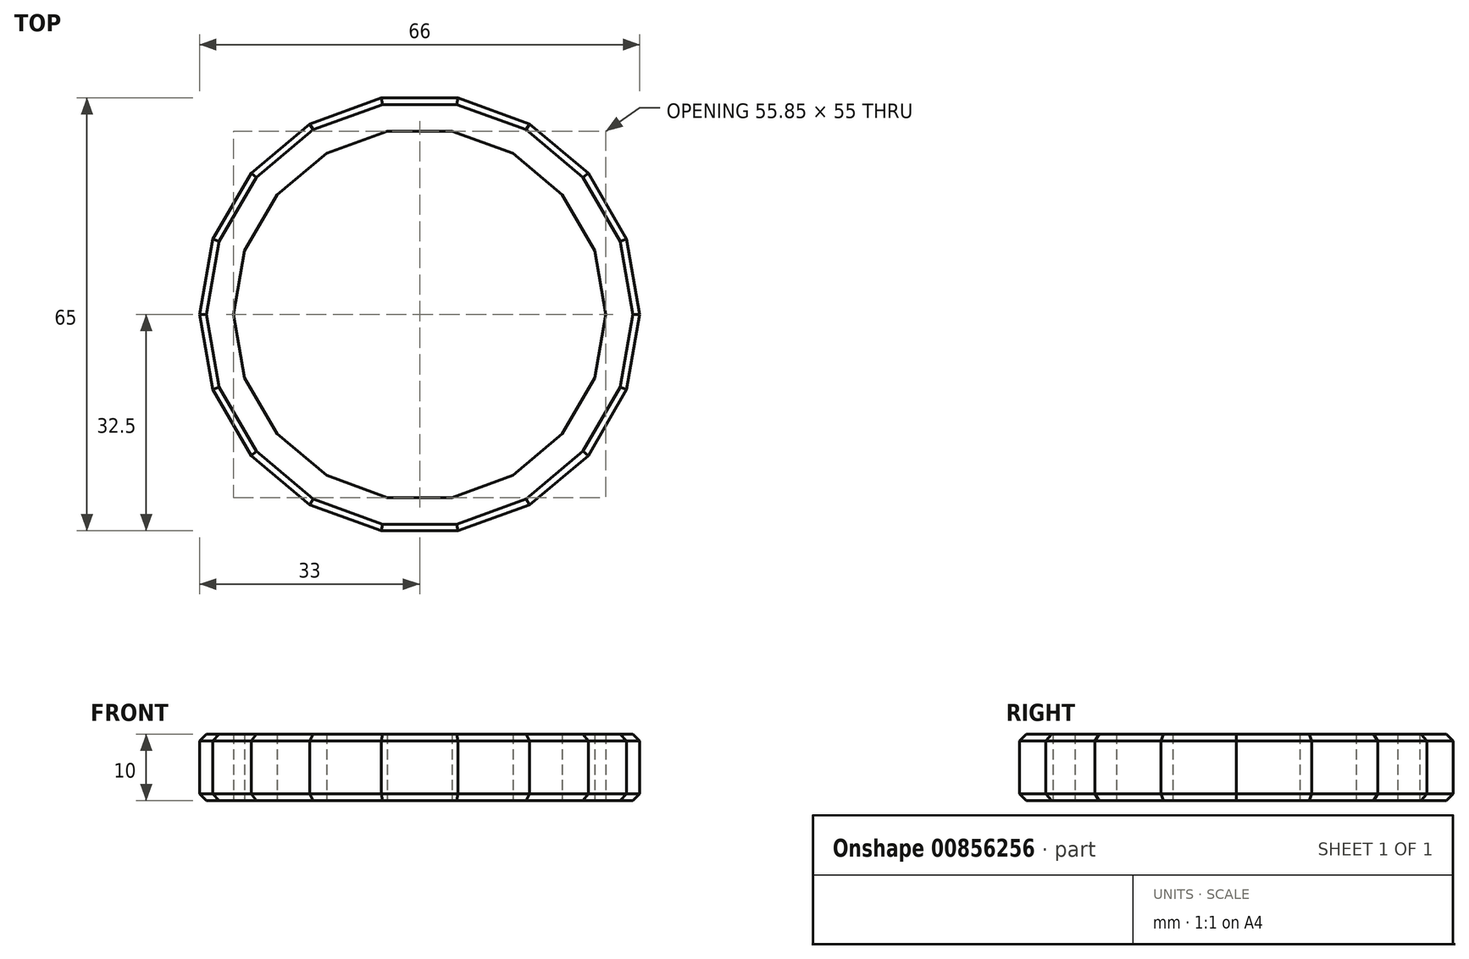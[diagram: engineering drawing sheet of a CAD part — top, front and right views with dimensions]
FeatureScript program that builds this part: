
annotation { "Feature Type Name" : "Feature", "Feature Type Description" : "" }
export const myFeature = defineFeature(function(context is Context, id is Id, definition is map)
    precondition{}
    {
        {
            var Q0;
            Q0=qCreatedBy(makeId("Top.planeOp"),FACE);
            var sketch = newSketch(context, id + "F0", { "sketchPlane" : qUnion([Q0])});
            skCircle(sketch, "E0.cCircle", {"center": v(0, 0) * mm, "radius": 27.5 * mm, "construction": true});
            skLineSegment(sketch, "E0.0", {"start": v(-4.85, 27.5) * mm, "end": v(4.85, 27.5) * mm});
            skLineSegment(sketch, "E0.1", {"start": v(4.85, 27.5) * mm, "end": v(13.96, 24.18) * mm});
            skLineSegment(sketch, "E0.2", {"start": v(13.96, 24.18) * mm, "end": v(21.4, 17.95) * mm});
            skLineSegment(sketch, "E0.3", {"start": v(21.4, 17.95) * mm, "end": v(26.24, 9.55) * mm});
            skLineSegment(sketch, "E0.4", {"start": v(26.24, 9.55) * mm, "end": v(27.92, 0) * mm});
            skLineSegment(sketch, "E0.5", {"start": v(27.92, 0) * mm, "end": v(26.24, -9.55) * mm});
            skLineSegment(sketch, "E0.6", {"start": v(26.24, -9.55) * mm, "end": v(21.4, -17.95) * mm});
            skLineSegment(sketch, "E0.7", {"start": v(21.4, -17.95) * mm, "end": v(13.96, -24.18) * mm});
            skLineSegment(sketch, "E0.8", {"start": v(13.96, -24.18) * mm, "end": v(4.85, -27.5) * mm});
            skLineSegment(sketch, "E0.9", {"start": v(4.85, -27.5) * mm, "end": v(-4.85, -27.5) * mm});
            skLineSegment(sketch, "E0.10", {"start": v(-4.85, -27.5) * mm, "end": v(-13.96, -24.18) * mm});
            skLineSegment(sketch, "E0.11", {"start": v(-13.96, -24.18) * mm, "end": v(-21.4, -17.95) * mm});
            skLineSegment(sketch, "E0.12", {"start": v(-21.4, -17.95) * mm, "end": v(-26.24, -9.55) * mm});
            skLineSegment(sketch, "E0.13", {"start": v(-26.24, -9.55) * mm, "end": v(-27.92, 0) * mm});
            skLineSegment(sketch, "E0.14", {"start": v(-27.92, 0) * mm, "end": v(-26.24, 9.55) * mm});
            skLineSegment(sketch, "E0.15", {"start": v(-26.24, 9.55) * mm, "end": v(-21.4, 17.95) * mm});
            skLineSegment(sketch, "E0.16", {"start": v(-21.4, 17.95) * mm, "end": v(-13.96, 24.18) * mm});
            skLineSegment(sketch, "E0.17", {"start": v(-13.96, 24.18) * mm, "end": v(-4.85, 27.5) * mm});
            skPoint(sketch, "E0.0.midPoint", {"position": v(0, 27.5) * mm});
            skCircle(sketch, "E1.cCircle", {"center": v(0, 0) * mm, "radius": 32.5 * mm, "construction": true});
            skLineSegment(sketch, "E1.0", {"start": v(-5.73, 32.5) * mm, "end": v(5.73, 32.5) * mm});
            skLineSegment(sketch, "E1.1", {"start": v(5.73, 32.5) * mm, "end": v(16.5, 28.58) * mm});
            skLineSegment(sketch, "E1.2", {"start": v(16.5, 28.58) * mm, "end": v(25.28, 21.21) * mm});
            skLineSegment(sketch, "E1.3", {"start": v(25.28, 21.21) * mm, "end": v(31.01, 11.29) * mm});
            skLineSegment(sketch, "E1.4", {"start": v(31.01, 11.29) * mm, "end": v(33, 0) * mm});
            skLineSegment(sketch, "E1.5", {"start": v(33, 0) * mm, "end": v(31.01, -11.29) * mm});
            skLineSegment(sketch, "E1.6", {"start": v(31.01, -11.29) * mm, "end": v(25.28, -21.21) * mm});
            skLineSegment(sketch, "E1.7", {"start": v(25.28, -21.21) * mm, "end": v(16.5, -28.58) * mm});
            skLineSegment(sketch, "E1.8", {"start": v(16.5, -28.58) * mm, "end": v(5.73, -32.5) * mm});
            skLineSegment(sketch, "E1.9", {"start": v(5.73, -32.5) * mm, "end": v(-5.73, -32.5) * mm});
            skLineSegment(sketch, "E1.10", {"start": v(-5.73, -32.5) * mm, "end": v(-16.5, -28.58) * mm});
            skLineSegment(sketch, "E1.11", {"start": v(-16.5, -28.58) * mm, "end": v(-25.28, -21.21) * mm});
            skLineSegment(sketch, "E1.12", {"start": v(-25.28, -21.21) * mm, "end": v(-31.01, -11.29) * mm});
            skLineSegment(sketch, "E1.13", {"start": v(-31.01, -11.29) * mm, "end": v(-33, 0) * mm});
            skLineSegment(sketch, "E1.14", {"start": v(-33, 0) * mm, "end": v(-31.01, 11.29) * mm});
            skLineSegment(sketch, "E1.15", {"start": v(-31.01, 11.29) * mm, "end": v(-25.28, 21.21) * mm});
            skLineSegment(sketch, "E1.16", {"start": v(-25.28, 21.21) * mm, "end": v(-16.5, 28.58) * mm});
            skLineSegment(sketch, "E1.17", {"start": v(-16.5, 28.58) * mm, "end": v(-5.73, 32.5) * mm});
            skPoint(sketch, "E1.0.midPoint", {"position": v(0, 32.5) * mm});
            skSolve(sketch);
        }
        {
            var Q0;
            Q0 = qSketchRegion(id + "F0", true);
            extrude(context, id + "F1", {"entities" : qUnion([Q0]), "depth" : 10 * mm, "offsetDistance" : 25.4 * mm});
        }
        {
            var Q0;
            Q0=makeQuery(id+"F1.opExtrude","CAP_EDGE",EDGE,{"disambiguationData":[OSD([sQuery(id+"F0.wireOp",EDGE,"E1.16")])],"isStart":false});
            var Q1;
            Q1=makeQuery(id+"F1.opExtrude","CAP_EDGE",EDGE,{"disambiguationData":[OSD([sQuery(id+"F0.wireOp",EDGE,"E1.17")])],"isStart":false});
            var Q2;
            Q2=makeQuery(id+"F1.opExtrude","CAP_EDGE",EDGE,{"disambiguationData":[OSD([sQuery(id+"F0.wireOp",EDGE,"E1.0")])],"isStart":false});
            var Q3;
            Q3=makeQuery(id+"F1.opExtrude","CAP_EDGE",EDGE,{"disambiguationData":[OSD([sQuery(id+"F0.wireOp",EDGE,"E1.1")])],"isStart":false});
            var Q4;
            Q4=makeQuery(id+"F1.opExtrude","CAP_EDGE",EDGE,{"disambiguationData":[OSD([sQuery(id+"F0.wireOp",EDGE,"E1.2")])],"isStart":false});
            var Q5;
            Q5=makeQuery(id+"F1.opExtrude","CAP_EDGE",EDGE,{"disambiguationData":[OSD([sQuery(id+"F0.wireOp",EDGE,"E1.3")])],"isStart":false});
            var Q6;
            Q6=makeQuery(id+"F1.opExtrude","CAP_EDGE",EDGE,{"disambiguationData":[OSD([sQuery(id+"F0.wireOp",EDGE,"E1.4")])],"isStart":false});
            var Q7;
            Q7=makeQuery(id+"F1.opExtrude","CAP_EDGE",EDGE,{"disambiguationData":[OSD([sQuery(id+"F0.wireOp",EDGE,"E1.5")])],"isStart":false});
            var Q8;
            Q8=makeQuery(id+"F1.opExtrude","CAP_EDGE",EDGE,{"disambiguationData":[OSD([sQuery(id+"F0.wireOp",EDGE,"E1.6")])],"isStart":false});
            var Q9;
            Q9=makeQuery(id+"F1.opExtrude","CAP_EDGE",EDGE,{"disambiguationData":[OSD([sQuery(id+"F0.wireOp",EDGE,"E1.7")])],"isStart":false});
            var Q10;
            Q10=makeQuery(id+"F1.opExtrude","CAP_EDGE",EDGE,{"disambiguationData":[OSD([sQuery(id+"F0.wireOp",EDGE,"E1.8")])],"isStart":false});
            var Q11;
            Q11=makeQuery(id+"F1.opExtrude","CAP_EDGE",EDGE,{"disambiguationData":[OSD([sQuery(id+"F0.wireOp",EDGE,"E1.9")])],"isStart":false});
            var Q12;
            Q12=makeQuery(id+"F1.opExtrude","CAP_EDGE",EDGE,{"disambiguationData":[OSD([sQuery(id+"F0.wireOp",EDGE,"E1.10")])],"isStart":false});
            var Q13;
            Q13=makeQuery(id+"F1.opExtrude","CAP_EDGE",EDGE,{"disambiguationData":[OSD([sQuery(id+"F0.wireOp",EDGE,"E1.11")])],"isStart":false});
            var Q14;
            Q14=makeQuery(id+"F1.opExtrude","CAP_EDGE",EDGE,{"disambiguationData":[OSD([sQuery(id+"F0.wireOp",EDGE,"E1.12")])],"isStart":false});
            var Q15;
            Q15=makeQuery(id+"F1.opExtrude","CAP_EDGE",EDGE,{"disambiguationData":[OSD([sQuery(id+"F0.wireOp",EDGE,"E1.13")])],"isStart":false});
            var Q16;
            Q16=makeQuery(id+"F1.opExtrude","CAP_EDGE",EDGE,{"disambiguationData":[OSD([sQuery(id+"F0.wireOp",EDGE,"E1.14")])],"isStart":false});
            var Q17;
            Q17=makeQuery(id+"F1.opExtrude","CAP_EDGE",EDGE,{"disambiguationData":[OSD([sQuery(id+"F0.wireOp",EDGE,"E1.15")])],"isStart":false});
            var Q18;
            Q18=makeQuery(id+"F1.opExtrude","CAP_EDGE",EDGE,{"disambiguationData":[OSD([sQuery(id+"F0.wireOp",EDGE,"E1.14")])],"isStart":true});
            var Q19;
            Q19=makeQuery(id+"F1.opExtrude","CAP_EDGE",EDGE,{"disambiguationData":[OSD([sQuery(id+"F0.wireOp",EDGE,"E1.15")])],"isStart":true});
            var Q20;
            Q20=makeQuery(id+"F1.opExtrude","CAP_EDGE",EDGE,{"disambiguationData":[OSD([sQuery(id+"F0.wireOp",EDGE,"E1.16")])],"isStart":true});
            var Q21;
            Q21=makeQuery(id+"F1.opExtrude","CAP_EDGE",EDGE,{"disambiguationData":[OSD([sQuery(id+"F0.wireOp",EDGE,"E1.17")])],"isStart":true});
            var Q22;
            Q22=makeQuery(id+"F1.opExtrude","CAP_EDGE",EDGE,{"disambiguationData":[OSD([sQuery(id+"F0.wireOp",EDGE,"E1.13")])],"isStart":true});
            var Q23;
            Q23=makeQuery(id+"F1.opExtrude","CAP_EDGE",EDGE,{"disambiguationData":[OSD([sQuery(id+"F0.wireOp",EDGE,"E1.12")])],"isStart":true});
            var Q24;
            Q24=makeQuery(id+"F1.opExtrude","CAP_EDGE",EDGE,{"disambiguationData":[OSD([sQuery(id+"F0.wireOp",EDGE,"E1.11")])],"isStart":true});
            var Q25;
            Q25=makeQuery(id+"F1.opExtrude","CAP_EDGE",EDGE,{"disambiguationData":[OSD([sQuery(id+"F0.wireOp",EDGE,"E1.10")])],"isStart":true});
            var Q26;
            Q26=makeQuery(id+"F1.opExtrude","CAP_EDGE",EDGE,{"disambiguationData":[OSD([sQuery(id+"F0.wireOp",EDGE,"E1.9")])],"isStart":true});
            var Q27;
            Q27=makeQuery(id+"F1.opExtrude","CAP_EDGE",EDGE,{"disambiguationData":[OSD([sQuery(id+"F0.wireOp",EDGE,"E1.8")])],"isStart":true});
            var Q28;
            Q28=makeQuery(id+"F1.opExtrude","CAP_EDGE",EDGE,{"disambiguationData":[OSD([sQuery(id+"F0.wireOp",EDGE,"E1.7")])],"isStart":true});
            var Q29;
            Q29=makeQuery(id+"F1.opExtrude","CAP_EDGE",EDGE,{"disambiguationData":[OSD([sQuery(id+"F0.wireOp",EDGE,"E1.6")])],"isStart":true});
            var Q30;
            Q30=makeQuery(id+"F1.opExtrude","CAP_EDGE",EDGE,{"disambiguationData":[OSD([sQuery(id+"F0.wireOp",EDGE,"E1.5")])],"isStart":true});
            var Q31;
            Q31=makeQuery(id+"F1.opExtrude","CAP_EDGE",EDGE,{"disambiguationData":[OSD([sQuery(id+"F0.wireOp",EDGE,"E1.4")])],"isStart":true});
            var Q32;
            Q32=makeQuery(id+"F1.opExtrude","CAP_EDGE",EDGE,{"disambiguationData":[OSD([sQuery(id+"F0.wireOp",EDGE,"E1.3")])],"isStart":true});
            var Q33;
            Q33=makeQuery(id+"F1.opExtrude","CAP_EDGE",EDGE,{"disambiguationData":[OSD([sQuery(id+"F0.wireOp",EDGE,"E1.2")])],"isStart":true});
            var Q34;
            Q34=makeQuery(id+"F1.opExtrude","CAP_EDGE",EDGE,{"disambiguationData":[OSD([sQuery(id+"F0.wireOp",EDGE,"E1.1")])],"isStart":true});
            var Q35;
            Q35=makeQuery(id+"F1.opExtrude","CAP_EDGE",EDGE,{"disambiguationData":[OSD([sQuery(id+"F0.wireOp",EDGE,"E1.0")])],"isStart":true});
            chamfer(context, id + "F2", {"entities" : qUnion([Q0, Q1, Q2, Q3, Q4, Q5, Q6, Q7, Q8, Q9, Q10, Q11, Q12, Q13, Q14, Q15, Q16, Q17, Q18, Q19, Q20, Q21, Q22, Q23, Q24, Q25, Q26, Q27, Q28, Q29, Q30, Q31, Q32, Q33, Q34, Q35]), "width" : 1 * mm, "tangentPropagation" : true});
        }
    });
